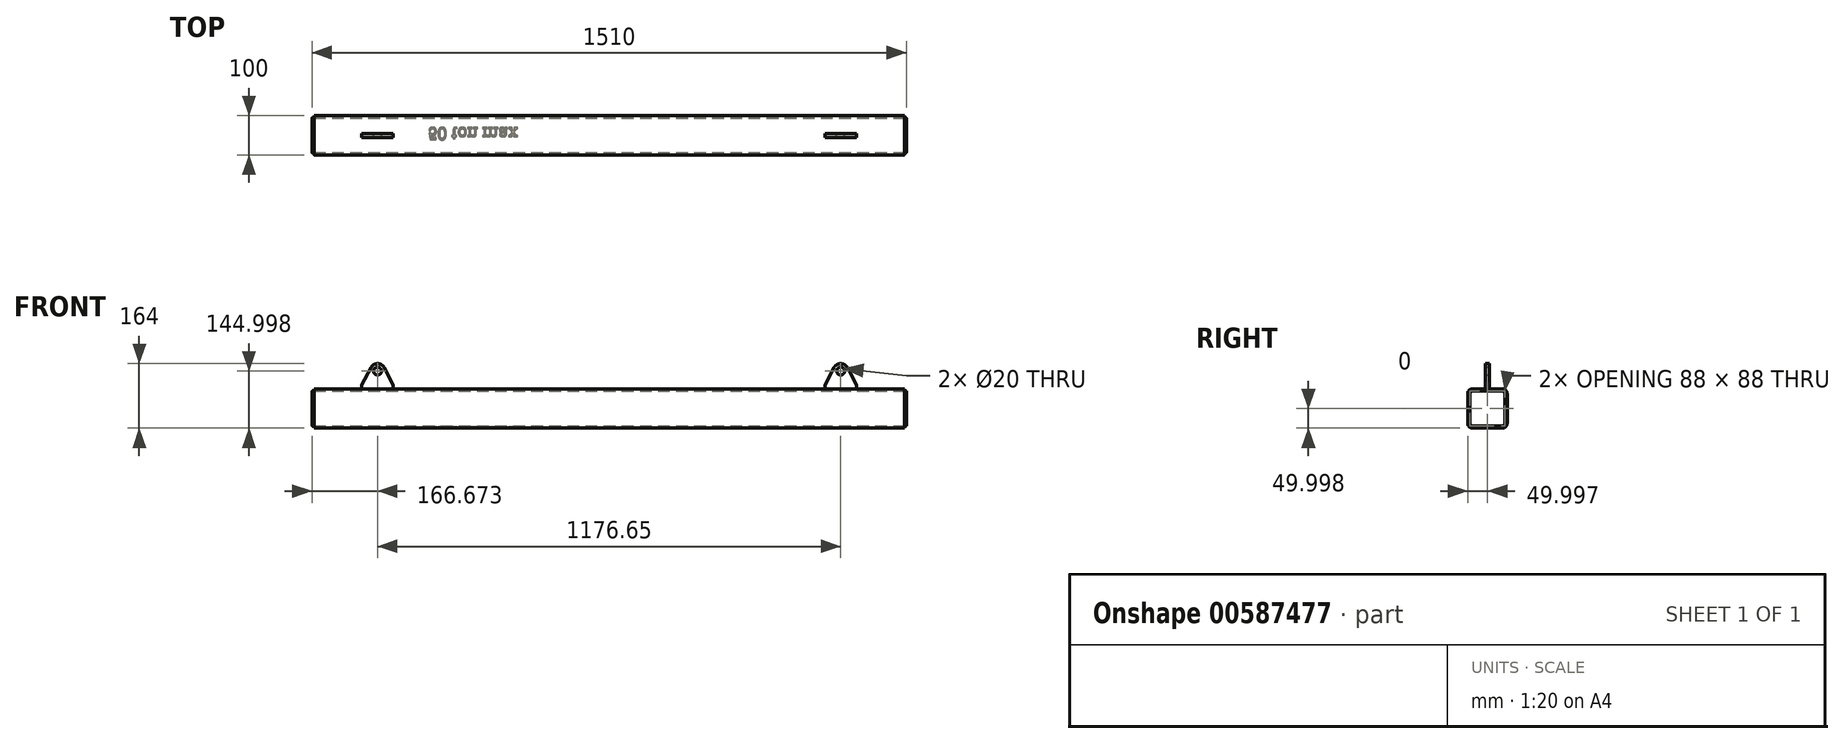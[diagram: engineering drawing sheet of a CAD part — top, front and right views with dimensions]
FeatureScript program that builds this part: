
annotation { "Feature Type Name" : "Feature", "Feature Type Description" : "" }
export const myFeature = defineFeature(function(context is Context, id is Id, definition is map)
    precondition{}
    {
        {
            var Q0;
            Q0=qCreatedBy(makeId("Right.planeOp"),FACE);
            var sketch = newSketch(context, id + "F0", { "sketchPlane" : qUnion([Q0])});
            skLineSegment(sketch, "E0.bottom", {"start": v(-63.03, 45.25) * mm, "end": v(12.97, 45.25) * mm});
            skLineSegment(sketch, "E0.top", {"start": v(-63.03, -42.75) * mm, "end": v(12.97, -42.75) * mm});
            skLineSegment(sketch, "E0.left", {"start": v(-69.03, 39.25) * mm, "end": v(-69.03, -36.75) * mm});
            skLineSegment(sketch, "E0.right", {"start": v(18.97, 39.25) * mm, "end": v(18.97, -36.75) * mm});
            skPoint(sketch, "E1.visualSharp", {"position": v(-69.03, 45.25) * mm});
            skArc(sketch, "E1.filletArc", {"start": v(-63.03, 45.25) * mm, "mid": v(-67.28, 43.5) * mm, "end": v(-69.03, 39.25) * mm});
            skPoint(sketch, "E2.visualSharp", {"position": v(18.97, 45.25) * mm});
            skArc(sketch, "E2.filletArc", {"start": v(18.97, 39.25) * mm, "mid": v(17.2, 43.5) * mm, "end": v(12.97, 45.25) * mm});
            skPoint(sketch, "E3.visualSharp", {"position": v(18.97, -42.75) * mm});
            skArc(sketch, "E3.filletArc", {"start": v(12.97, -42.75) * mm, "mid": v(17.2, -41) * mm, "end": v(18.97, -36.75) * mm});
            skPoint(sketch, "E4.visualSharp", {"position": v(-69.03, -42.75) * mm});
            skArc(sketch, "E4.filletArc", {"start": v(-69.03, -36.75) * mm, "mid": v(-67.28, -41) * mm, "end": v(-63.03, -42.75) * mm});
            skArc(sketch, "E5.0", {"start": v(-63.03, 51.25) * mm, "mid": v(-71.52, 47.73) * mm, "end": v(-75.03, 39.25) * mm});
            skLineSegment(sketch, "E5.1", {"start": v(-75.03, 39.25) * mm, "end": v(-75.03, -36.75) * mm});
            skLineSegment(sketch, "E5.2", {"start": v(-63.03, 51.25) * mm, "end": v(12.97, 51.25) * mm});
            skArc(sketch, "E5.3", {"start": v(-75.03, -36.75) * mm, "mid": v(-71.52, -45.24) * mm, "end": v(-63.03, -48.75) * mm});
            skArc(sketch, "E5.4", {"start": v(24.97, 39.25) * mm, "mid": v(21.45, 47.73) * mm, "end": v(12.97, 51.25) * mm});
            skLineSegment(sketch, "E5.5", {"start": v(24.97, 39.25) * mm, "end": v(24.97, -36.75) * mm});
            skArc(sketch, "E5.6", {"start": v(12.97, -48.75) * mm, "mid": v(21.45, -45.24) * mm, "end": v(24.97, -36.75) * mm});
            skLineSegment(sketch, "E5.7", {"start": v(-63.03, -48.75) * mm, "end": v(12.97, -48.75) * mm});
            skSolve(sketch);
        }
        {
            var Q0;
            Q0=makeQuery(id+"F0.imprint","IMPRINT",FACE,{"disambiguationData":[TD([[makeQuery(id+"F0.imprint","IMPRINT",EDGE,{"derivedFrom":sQuery(id+"F0.wireOp",EDGE,"E0.bottom")}),1.0]])]});
            extrude(context, id + "F1", {"entities" : qUnion([Q0]), "depth" : 1500 * mm, "offsetDistance" : 25 * mm});
        }
        {
            var Q0;
            Q0=makeQuery(id+"F1.opExtrude","CAP_FACE",FACE,{"disambiguationData":[OSD([sQuery(id+"F0.wireOp",EDGE,"E0.bottom"),sQuery(id+"F0.wireOp",EDGE,"E0.top"),sQuery(id+"F0.wireOp",EDGE,"E0.left"),sQuery(id+"F0.wireOp",EDGE,"E0.right"),sQuery(id+"F0.wireOp",EDGE,"E1.filletArc"),sQuery(id+"F0.wireOp",EDGE,"E2.filletArc"),sQuery(id+"F0.wireOp",EDGE,"E3.filletArc"),sQuery(id+"F0.wireOp",EDGE,"E4.filletArc"),sQuery(id+"F0.wireOp",EDGE,"E5.0"),sQuery(id+"F0.wireOp",EDGE,"E5.1"),sQuery(id+"F0.wireOp",EDGE,"E5.2"),sQuery(id+"F0.wireOp",EDGE,"E5.3"),sQuery(id+"F0.wireOp",EDGE,"E5.4"),sQuery(id+"F0.wireOp",EDGE,"E5.5"),sQuery(id+"F0.wireOp",EDGE,"E5.6"),sQuery(id+"F0.wireOp",EDGE,"E5.7")])],"isStart":false});
            var sketch = newSketch(context, id + "F2", { "sketchPlane" : qUnion([Q0])});
            skPoint(sketch, "E6.0", {"position": v(-25.03, 51.25) * mm});
            skSolve(sketch);
        }
        {
            var Q0;
            Q0=sQuery(id+"F2.wireOp",VERTEX,"E6.0");
            var Q1;
            Q1=makeQuery(id+"F1.opExtrude","SWEPT_FACE",FACE,{"disambiguationData":[OSD([sQuery(id+"F0.wireOp",EDGE,"E5.1")])]});
            cPlane(context, id + "F3", {"entities" : qUnion([Q0, Q1]), "cplaneType" : CPlaneType.PLANE_POINT, "offset" : 25 * mm, "width" : 150 * mm, "height" : 150 * mm});
        }
        {
            var Q0;
            Q0=qCreatedBy(id+"F3.planeOp",FACE);
            var sketch = newSketch(context, id + "F4", { "sketchPlane" : qUnion([Q0])});
            skLineSegment(sketch, "E7.0", {"start": v(1500, 51.25) * mm, "end": v(0, 51.25) * mm});
            skCircle(sketch, "E8", {"center": v(838.33, 96.25) * mm, "radius": 10 * mm});
            skArc(sketch, "E9", {"start": v(855.12, 105.13) * mm, "mid": v(838.33, 115.25) * mm, "end": v(821.53, 105.13) * mm});
            skLineSegment(sketch, "E10", {"start": v(838.33, 96.25) * mm, "end": v(838.33, 51.25) * mm});
            skLineSegment(sketch, "E11", {"start": v(878.33, 51.25) * mm, "end": v(878.33, 61.25) * mm});
            skLineSegment(sketch, "E12", {"start": v(878.33, 61.25) * mm, "end": v(855.12, 105.13) * mm});
            skLineSegment(sketch, "E13.MirrorCS", {"start": v(798.33, 61.25) * mm, "end": v(821.53, 105.13) * mm});
            skLineSegment(sketch, "E14.MirrorCS", {"start": v(798.33, 51.25) * mm, "end": v(798.33, 61.25) * mm});
            skSolve(sketch);
        }
        {
            var Q0;
            Q0=makeQuery(id+"F4.imprint","IMPRINT",FACE,{"disambiguationData":[TD([[makeQuery(id+"F4.imprint","IMPRINT",EDGE,{"derivedFrom":sQuery(id+"F4.wireOp",EDGE,"E8")}),-1.0]])]});
            extrude(context, id + "F5", {"entities" : qUnion([Q0]), "endBound" : BoundingType.SYMMETRIC, "depth" : 10 * mm, "offsetDistance" : 25 * mm});
        }
        {
            var Q0;
            Q0=makeQuery(id+"F1.opExtrude","SWEPT_EDGE",EDGE,{"disambiguationData":[OSD([sQuery(id+"F0.wireOp",EDGE,"E5.0"),sQuery(id+"F0.wireOp",EDGE,"E5.2")])]});
            cPoint(context, id + "F6", {"entities" : qUnion([Q0]), "parameter" : 0.5});
        }
        {
            var Q0;
            Q0 = qCreatedBy(id + "F6" ,VERTEX);
            var Q1;
            Q1=qCreatedBy(makeId("Right.planeOp"),FACE);
            cPlane(context, id + "F7", {"entities" : qUnion([Q0, Q1]), "cplaneType" : CPlaneType.PLANE_POINT, "offset" : 25 * mm, "width" : 150 * mm, "height" : 150 * mm});
        }
        {
            var Q0;
            Q0=makeQuery(id+"F5.opExtrude","SWEPT_BODY",BODY,{"disambiguationData":[OSD([sQuery(id+"F4.wireOp",EDGE,"E7.0"),sQuery(id+"F4.wireOp",EDGE,"E8"),sQuery(id+"F4.wireOp",EDGE,"E9"),sQuery(id+"F4.wireOp",EDGE,"E11"),sQuery(id+"F4.wireOp",EDGE,"E12"),sQuery(id+"F4.wireOp",EDGE,"E13.MirrorCS"),sQuery(id+"F4.wireOp",EDGE,"E14.MirrorCS")])]});
            var Q1;
            Q1=makeQuery(id+"F1.opExtrude","SWEPT_EDGE",EDGE,{"disambiguationData":[OSD([sQuery(id+"F0.wireOp",EDGE,"E5.0"),sQuery(id+"F0.wireOp",EDGE,"E5.2")])]});
            var Q2;
            Q2=makeQuery(id+"F1.opExtrude","SWEPT_EDGE",EDGE,{"disambiguationData":[OSD([sQuery(id+"F0.wireOp",EDGE,"E5.0"),sQuery(id+"F0.wireOp",EDGE,"E5.2")])]});
            transform(context, id + "F8", {"entities" : qUnion([Q0]), "transformType" : TransformType.TRANSLATION_DISTANCE, "transformDirection" : qUnion([Q2]), "distance" : 500 * mm, "oppositeDirection" : true, "makeCopy" : false});
        }
        {
            var Q0;
            Q0=makeQuery(id+"F5.opExtrude","SWEPT_BODY",BODY,{"disambiguationData":[OSD([sQuery(id+"F4.wireOp",EDGE,"E7.0"),sQuery(id+"F4.wireOp",EDGE,"E8"),sQuery(id+"F4.wireOp",EDGE,"E9"),sQuery(id+"F4.wireOp",EDGE,"E11"),sQuery(id+"F4.wireOp",EDGE,"E12"),sQuery(id+"F4.wireOp",EDGE,"E13.MirrorCS"),sQuery(id+"F4.wireOp",EDGE,"E14.MirrorCS")])]});
            var Q1;
            Q1=makeQuery(id+"F1.opExtrude","SWEPT_BODY",BODY,{"disambiguationData":[OSD([sQuery(id+"F0.wireOp",EDGE,"E0.bottom"),sQuery(id+"F0.wireOp",EDGE,"E0.top"),sQuery(id+"F0.wireOp",EDGE,"E0.left"),sQuery(id+"F0.wireOp",EDGE,"E0.right"),sQuery(id+"F0.wireOp",EDGE,"E1.filletArc"),sQuery(id+"F0.wireOp",EDGE,"E2.filletArc"),sQuery(id+"F0.wireOp",EDGE,"E3.filletArc"),sQuery(id+"F0.wireOp",EDGE,"E4.filletArc"),sQuery(id+"F0.wireOp",EDGE,"E5.0"),sQuery(id+"F0.wireOp",EDGE,"E5.1"),sQuery(id+"F0.wireOp",EDGE,"E5.2"),sQuery(id+"F0.wireOp",EDGE,"E5.3"),sQuery(id+"F0.wireOp",EDGE,"E5.4"),sQuery(id+"F0.wireOp",EDGE,"E5.5"),sQuery(id+"F0.wireOp",EDGE,"E5.6"),sQuery(id+"F0.wireOp",EDGE,"E5.7")])]});
            var Q2;
            Q2=qCreatedBy(id+"F7.planeOp",FACE);
            mirror(context, id + "F9", {"entities" : qUnion([Q0, Q1]), "mirrorPlane" : qUnion([Q2])});
        }
        {
            var Q0;
            Q0=makeQuery(id+"F1.opExtrude","CAP_FACE",FACE,{"disambiguationData":[OSD([sQuery(id+"F0.wireOp",EDGE,"E0.bottom"),sQuery(id+"F0.wireOp",EDGE,"E0.top"),sQuery(id+"F0.wireOp",EDGE,"E0.left"),sQuery(id+"F0.wireOp",EDGE,"E0.right"),sQuery(id+"F0.wireOp",EDGE,"E1.filletArc"),sQuery(id+"F0.wireOp",EDGE,"E2.filletArc"),sQuery(id+"F0.wireOp",EDGE,"E3.filletArc"),sQuery(id+"F0.wireOp",EDGE,"E4.filletArc"),sQuery(id+"F0.wireOp",EDGE,"E5.0"),sQuery(id+"F0.wireOp",EDGE,"E5.1"),sQuery(id+"F0.wireOp",EDGE,"E5.2"),sQuery(id+"F0.wireOp",EDGE,"E5.3"),sQuery(id+"F0.wireOp",EDGE,"E5.4"),sQuery(id+"F0.wireOp",EDGE,"E5.5"),sQuery(id+"F0.wireOp",EDGE,"E5.6"),sQuery(id+"F0.wireOp",EDGE,"E5.7")])],"isStart":true});
            var sketch = newSketch(context, id + "F10", { "sketchPlane" : qUnion([Q0])});
            skArc(sketch, "E15.0", {"start": v(63.03, 46.25) * mm, "mid": v(73.64, 41.85) * mm, "end": v(78.03, 31.25) * mm});
            skLineSegment(sketch, "E15.1", {"start": v(78.03, 31.25) * mm, "end": v(78.03, -48.75) * mm});
            skLineSegment(sketch, "E15.2", {"start": v(63.03, 46.25) * mm, "end": v(-16.97, 46.25) * mm});
            skArc(sketch, "E15.3", {"start": v(78.03, -48.75) * mm, "mid": v(73.64, -59.36) * mm, "end": v(63.03, -63.75) * mm});
            skArc(sketch, "E15.4", {"start": v(-31.97, 31.25) * mm, "mid": v(-27.57, 41.85) * mm, "end": v(-16.97, 46.25) * mm});
            skLineSegment(sketch, "E15.5", {"start": v(-31.97, 31.25) * mm, "end": v(-31.97, -48.75) * mm});
            skArc(sketch, "E15.6", {"start": v(-16.97, -63.75) * mm, "mid": v(-27.57, -59.36) * mm, "end": v(-31.97, -48.75) * mm});
            skLineSegment(sketch, "E15.7", {"start": v(63.03, -63.75) * mm, "end": v(-16.97, -63.75) * mm});
            skSolve(sketch);
        }
        {
            var Q0;
            Q0=makeQuery(id+"F10.imprint","IMPRINT",FACE,{"disambiguationData":[TD([[makeQuery(id+"F10.imprint","IMPRINT",EDGE,{"derivedFrom":makeQuery(id+"F1.opExtrude","CAP_EDGE",EDGE,{"disambiguationData":[OSD([sQuery(id+"F0.wireOp",EDGE,"E0.bottom")])],"isStart":true})}),1.0]])]});
            extrude(context, id + "F11", {"entities" : qUnion([Q0]), "depth" : 5 * mm, "offsetDistance" : 25 * mm});
        }
        {
            var Q0;
            Q0=makeQuery(id+"F11.opExtrude","SWEPT_BODY",BODY,{"disambiguationData":[OSD([sQuery(id+"F0.wireOp",EDGE,"E0.bottom"),sQuery(id+"F0.wireOp",EDGE,"E0.top"),sQuery(id+"F0.wireOp",EDGE,"E0.left"),sQuery(id+"F0.wireOp",EDGE,"E0.right"),sQuery(id+"F0.wireOp",EDGE,"E1.filletArc"),sQuery(id+"F0.wireOp",EDGE,"E2.filletArc"),sQuery(id+"F0.wireOp",EDGE,"E3.filletArc"),sQuery(id+"F0.wireOp",EDGE,"E4.filletArc")])]});
            var Q1;
            Q1=qCreatedBy(id+"F7.planeOp",FACE);
            mirror(context, id + "F12", {"entities" : qUnion([Q0]), "mirrorPlane" : qUnion([Q1])});
        }
        {
            var Q0;
            Q0=makeQuery(id+"F1.opExtrude","SWEPT_FACE",FACE,{"disambiguationData":[OSD([sQuery(id+"F0.wireOp",EDGE,"E5.7")])]});
            var sketch = newSketch(context, id + "F13", { "sketchPlane" : qUnion([Q0])});
            skText(sketch, "E16", { "text": "50 ton max", "fontName": "RobotoSlab-Regular.ttf"});
            const initialGuessF13  = {"E16": [0.29045, 0.00528, 1, 0, 0.03126]};
            skSetInitialGuess(sketch, initialGuessF13);
            skSolve(sketch);
        }
        {
            var Q0;
            Q0 = qSketchRegion(id + "F13", true);
            extrude(context, id + "F14", {"entities" : qUnion([Q0]), "operationType" : NewBodyOperationType.REMOVE, "oppositeDirection" : true, "depth" : 3 * mm, "offsetDistance" : 25 * mm});
        }
    });
